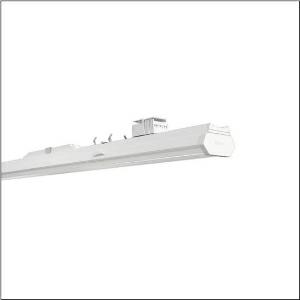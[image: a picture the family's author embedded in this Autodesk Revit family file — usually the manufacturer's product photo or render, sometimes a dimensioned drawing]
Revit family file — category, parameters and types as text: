
# Revit family: licross_r__11_protected_ho_51td11dn4f5s_b27d
name_source: partatom
category: Lighting Fixtures
units: mm (PartAtom-declared; Revit-internal decimal feet)

## family parameters
Cut with Voids When Loaded = No
Host = Face
Light Source = No
Part Type = Normal
Room Calculation Point = No
Round Connector Dimension = Use Diameter
Shared = No

## types (1)
- --- (1 x LED, 15510 lm, 87.3 W, 4000K)
    Apparent Load = 87 VA
    CIE Flux Codes = 84 94 98 99 100
    Color Rendering = 80
    Color Temperature = 4000K
    Default Elevation = 1800 mm
    Description = Licross® 11 Protected HO, luminaire insert, of sheet steel, galvanised, coil coated, white, length: 1.500mm, width: 90mm, height: 101mm, LED rated luminous flux: 15.510lm, light colour: 840, control gear: DALI 2, control gear: ECG DALI, with plug, 5-pole, with phase selection, mains connection: 220..240V, AC, 50/60Hz, halogen-free wiring, primary light control with lens, of plastic, primary optical cover: cover, of PMMA, light emission: direct with ceiling illumination distribution, primary light characteristic: symmetric, protection rating (complete): IP54, insulation class (complete): insulation class I (protective earthing), certification: CE, ENEC, VDE, UKCA, protection symbol: D if used in an environment with non-conductive dust loads with corresponding accessories, impact resistance: IK06, permissible ambient temperature for indoor applications: -25..+30°C, corresponds to IFS (International Featured Standards) requirements for safety and quality in the food industry, reducing of maximum allowable ambient temperature of 5°C with ceiling mounting, LABS conformity tested according to VDMA 24364:2018-05, packaging unit: 1 piece
    Height = 92 mm
    Lamp = 1 x LED
    Lamp Light Flux = 15510 lm
    Lamp Power = 87.3 W
    Lamp count = 1
    Length = 1500 mm
    Luminous efficacy = 178 lm/W
    Manufacturer = Siteco
    ModVariant = No
    Model = 51TD11DN4F5S
    Mounting Place = Ceiling
    Mounting Type = Pendant
    Number of Poles = 1
    OnlyDefault = Yes
    Power Factor = 1
    Product Name = Licross® 11 Protected HO
    Product group = luminaire insert
    ProductGroupID = 902
    Protection Class = Protection class I
    Protection Degree = IP 54
    RLX_Detail_Level = 1
    RlxData = <blob elided: 24365 chars, md5=2583af18>
    Socket = socket
    Standby Power = 0 W
    System Light Flux = 15510 lm
    System Power = 87 W
    Type Comments = factory setting: luminous flux: 100 % | dim-lin: 254 | 589 mA
    Type Image = l_1256145.jpg
    URL = http://relux.com
    VarID = @adj_010207
    Voltage = 0 V
    Weight = 0.00 kg
    Width = 88 mm

## geometry (parser evidence)
native form markers: Blend x4, Sweep x11
no freeform markers — native parametric forms only
